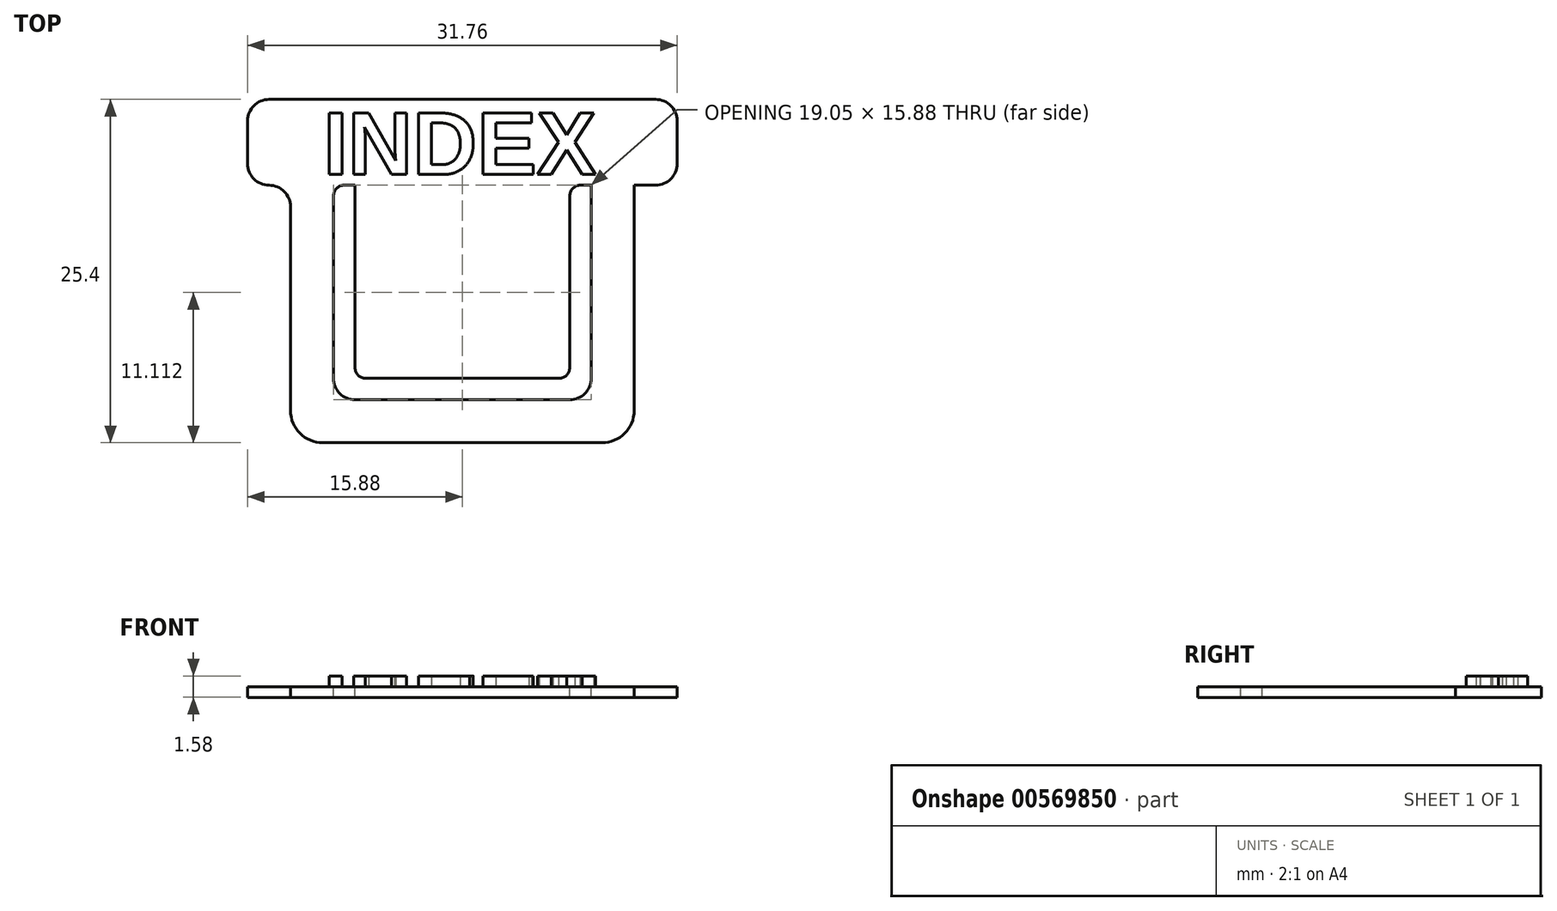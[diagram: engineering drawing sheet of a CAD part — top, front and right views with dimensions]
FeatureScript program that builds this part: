
annotation { "Feature Type Name" : "Feature", "Feature Type Description" : "" }
export const myFeature = defineFeature(function(context is Context, id is Id, definition is map)
    precondition{}
    {
        {
            var Q0;
            Q0=qCreatedBy(makeId("Front.planeOp"),FACE);
            var sketch = newSketch(context, id + "F0", { "sketchPlane" : qUnion([Q0])});
            skLineSegment(sketch, "E0.bottom", {"start": v(12.7, 9.53) * mm, "end": v(-12.7, 9.53) * mm});
            skLineSegment(sketch, "E0.top", {"start": v(12.7, -9.53) * mm, "end": v(-12.7, -9.53) * mm});
            skLineSegment(sketch, "E0.left", {"start": v(12.7, 9.53) * mm, "end": v(12.7, -9.53) * mm});
            skLineSegment(sketch, "E0.right", {"start": v(-12.7, 9.53) * mm, "end": v(-12.7, -9.53) * mm});
            skPoint(sketch, "E0.middle", {"position": v(0, 0) * mm});
            skSolve(sketch);
        }
        {
            var Q0;
            Q0=makeQuery(id+"F0.imprint","IMPRINT",FACE,{"disambiguationData":[TD([[makeQuery(id+"F0.imprint","IMPRINT",EDGE,{"derivedFrom":sQuery(id+"F0.wireOp",EDGE,"E0.bottom")}),1.0]])]});
            extrude(context, id + "F1", {"entities" : qUnion([Q0]), "depth" : 0.8 * mm, "offsetDistance" : 25.4 * mm});
        }
        {
            var Q0;
            Q0=makeQuery(id+"F1.opExtrude","SWEPT_EDGE",EDGE,{"disambiguationData":[OSD([sQuery(id+"F0.wireOp",EDGE,"E0.top"),sQuery(id+"F0.wireOp",EDGE,"E0.left")])]});
            var Q1;
            Q1=makeQuery(id+"F1.opExtrude","SWEPT_EDGE",EDGE,{"disambiguationData":[OSD([sQuery(id+"F0.wireOp",EDGE,"E0.top"),sQuery(id+"F0.wireOp",EDGE,"E0.right")])]});
            fillet(context, id + "F2", {"entities" : qUnion([Q0, Q1]), "radius" : 2.38 * mm, "tangentPropagation" : true, "allowEdgeOverflow" : false});
        }
        {
            var Q0;
            Q0=makeQuery(id+"F1.opExtrude","CAP_FACE",FACE,{"disambiguationData":[OSD([sQuery(id+"F0.wireOp",EDGE,"E0.bottom"),sQuery(id+"F0.wireOp",EDGE,"E0.top"),sQuery(id+"F0.wireOp",EDGE,"E0.left"),sQuery(id+"F0.wireOp",EDGE,"E0.right")])],"isStart":false});
            var sketch = newSketch(context, id + "F3", { "sketchPlane" : qUnion([Q0])});
            skLineSegment(sketch, "E1.bottom", {"start": v(9.52, 9.53) * mm, "end": v(-9.53, 9.53) * mm});
            skLineSegment(sketch, "E1.top", {"start": v(9.53, -6.35) * mm, "end": v(-9.53, -6.35) * mm});
            skLineSegment(sketch, "E1.left", {"start": v(9.52, 9.53) * mm, "end": v(9.53, -6.35) * mm});
            skLineSegment(sketch, "E1.right", {"start": v(-9.53, 9.53) * mm, "end": v(-9.52, -6.35) * mm});
            skPoint(sketch, "E1.middle", {"position": v(0, 0) * mm});
            skSolve(sketch);
        }
        {
            var Q0;
            Q0=makeQuery(id+"F3.imprint","IMPRINT",FACE,{"disambiguationData":[TD([[makeQuery(id+"F3.imprint","IMPRINT",EDGE,{"derivedFrom":sQuery(id+"F3.wireOp",EDGE,"E1.bottom")}),1.0]])]});
            extrude(context, id + "F4", {"entities" : qUnion([Q0]), "operationType" : NewBodyOperationType.REMOVE, "oppositeDirection" : true, "depth" : 4.93 * mm, "offsetDistance" : 25.4 * mm});
        }
        {
            var Q0;
            Q0=makeQuery(id+"F1.opExtrude","CAP_FACE",FACE,{"disambiguationData":[OSD([sQuery(id+"F0.wireOp",EDGE,"E0.bottom"),sQuery(id+"F0.wireOp",EDGE,"E0.top"),sQuery(id+"F0.wireOp",EDGE,"E0.left"),sQuery(id+"F0.wireOp",EDGE,"E0.right")])],"isStart":false});
            var sketch = newSketch(context, id + "F5", { "sketchPlane" : qUnion([Q0])});
            skLineSegment(sketch, "E2.bottom", {"start": v(-15.88, 9.53) * mm, "end": v(15.87, 9.53) * mm});
            skLineSegment(sketch, "E2.top", {"start": v(-15.88, 15.88) * mm, "end": v(15.87, 15.88) * mm});
            skLineSegment(sketch, "E2.left", {"start": v(-15.88, 9.53) * mm, "end": v(-15.88, 15.88) * mm});
            skLineSegment(sketch, "E2.right", {"start": v(15.87, 9.53) * mm, "end": v(15.87, 15.88) * mm});
            skSolve(sketch);
        }
        {
            var Q0;
            Q0=makeQuery(id+"F5.imprint","IMPRINT",FACE,{"disambiguationData":[TD([[makeQuery(id+"F5.imprint","IMPRINT",EDGE,{"derivedFrom":sQuery(id+"F5.wireOp",EDGE,"E2.top")}),-1.0]])]});
            extrude(context, id + "F6", {"entities" : qUnion([Q0]), "operationType" : NewBodyOperationType.ADD, "oppositeDirection" : true, "depth" : 0.8 * mm, "offsetDistance" : 25.4 * mm});
        }
        {
            var Q0;
            Q0=makeQuery(id+"F6.opExtrude","SWEPT_EDGE",EDGE,{"disambiguationData":[OSD([sQuery(id+"F5.wireOp",EDGE,"E2.top"),sQuery(id+"F5.wireOp",EDGE,"E2.left")])]});
            var Q1;
            Q1=makeQuery(id+"F6.opExtrude","SWEPT_EDGE",EDGE,{"disambiguationData":[OSD([sQuery(id+"F5.wireOp",EDGE,"E2.top"),sQuery(id+"F5.wireOp",EDGE,"E2.right")])]});
            var Q2;
            Q2=makeQuery(id+"F6.opExtrude","SWEPT_EDGE",EDGE,{"disambiguationData":[OSD([sQuery(id+"F5.wireOp",EDGE,"E2.bottom"),sQuery(id+"F5.wireOp",EDGE,"E2.right")])]});
            var Q3;
            Q3=makeQuery(id+"F1.opExtrude","SWEPT_EDGE",EDGE,{"disambiguationData":[OSD([sQuery(id+"F0.wireOp",EDGE,"E0.bottom"),sQuery(id+"F0.wireOp",EDGE,"E0.left")])]});
            var Q4;
            Q4=makeQuery(id+"F6.opExtrude","SWEPT_EDGE",EDGE,{"disambiguationData":[OSD([sQuery(id+"F5.wireOp",EDGE,"E2.bottom"),sQuery(id+"F5.wireOp",EDGE,"E2.left")])]});
            var Q5;
            Q5=makeQuery(id+"F1.opExtrude","SWEPT_EDGE",EDGE,{"disambiguationData":[OSD([sQuery(id+"F0.wireOp",EDGE,"E0.bottom"),sQuery(id+"F0.wireOp",EDGE,"E0.right")])]});
            fillet(context, id + "F7", {"entities" : qUnion([Q0, Q1, Q2, Q3, Q4, Q5]), "radius" : 1.59 * mm, "tangentPropagation" : true, "allowEdgeOverflow" : false});
        }
        {
            var Q0;
            Q0=makeQuery(id+"F4.boolean.opBoolean","COPY",EDGE,{"derivedFrom":makeQuery(id+"F4.opExtrude","SWEPT_EDGE",EDGE,{"disambiguationData":[OSD([sQuery(id+"F3.wireOp",EDGE,"E1.top"),sQuery(id+"F3.wireOp",EDGE,"E1.right")])]})});
            var Q1;
            Q1=makeQuery(id+"F4.boolean.opBoolean","COPY",EDGE,{"derivedFrom":makeQuery(id+"F4.opExtrude","SWEPT_EDGE",EDGE,{"disambiguationData":[OSD([sQuery(id+"F3.wireOp",EDGE,"E1.top"),sQuery(id+"F3.wireOp",EDGE,"E1.left")])]})});
            fillet(context, id + "F8", {"entities" : qUnion([Q0, Q1]), "radius" : 1.59 * mm, "tangentPropagation" : true, "allowEdgeOverflow" : false});
        }
        {
            var Q0;
            Q0=makeQuery(id+"F6.boolean.opBoolean","MERGE",FACE,{"derivedFrom":[makeQuery(id+"F1.opExtrude","CAP_FACE",FACE,{"disambiguationData":[OSD([sQuery(id+"F0.wireOp",EDGE,"E0.bottom"),sQuery(id+"F0.wireOp",EDGE,"E0.top"),sQuery(id+"F0.wireOp",EDGE,"E0.left"),sQuery(id+"F0.wireOp",EDGE,"E0.right")])],"isStart":false}),makeQuery(id+"F6.opExtrude","CAP_FACE",FACE,{"disambiguationData":[OSD([sQuery(id+"F5.wireOp",EDGE,"E2.bottom"),sQuery(id+"F5.wireOp",EDGE,"E2.top"),sQuery(id+"F5.wireOp",EDGE,"E2.left"),sQuery(id+"F5.wireOp",EDGE,"E2.right")])],"isStart":true})]});
            var sketch = newSketch(context, id + "F9", { "sketchPlane" : qUnion([Q0])});
            skLineSegment(sketch, "E3.bottom", {"start": v(-7.94, 9.53) * mm, "end": v(7.94, 9.53) * mm});
            skLineSegment(sketch, "E3.top", {"start": v(-7.94, -4.76) * mm, "end": v(7.94, -4.76) * mm});
            skLineSegment(sketch, "E3.left", {"start": v(-7.94, 9.53) * mm, "end": v(-7.94, -4.76) * mm});
            skLineSegment(sketch, "E3.right", {"start": v(7.94, 9.53) * mm, "end": v(7.94, -4.76) * mm});
            skSolve(sketch);
        }
        {
            var Q0;
            Q0=makeQuery(id+"F9.imprint","IMPRINT",FACE,{"disambiguationData":[TD([[makeQuery(id+"F9.imprint","IMPRINT",EDGE,{"derivedFrom":sQuery(id+"F9.wireOp",EDGE,"E3.bottom")}),1.0]])]});
            extrude(context, id + "F10", {"entities" : qUnion([Q0]), "operationType" : NewBodyOperationType.ADD, "oppositeDirection" : true, "depth" : 0.8 * mm, "offsetDistance" : 25.4 * mm});
        }
        {
            var Q0;
            Q0=makeQuery(id+"F10.boolean.opBoolean","MERGE",FACE,{"derivedFrom":[makeQuery(id+"F6.boolean.opBoolean","MERGE",FACE,{"derivedFrom":[makeQuery(id+"F1.opExtrude","CAP_FACE",FACE,{"disambiguationData":[OSD([sQuery(id+"F0.wireOp",EDGE,"E0.bottom"),sQuery(id+"F0.wireOp",EDGE,"E0.top"),sQuery(id+"F0.wireOp",EDGE,"E0.left"),sQuery(id+"F0.wireOp",EDGE,"E0.right")])],"isStart":false}),makeQuery(id+"F6.opExtrude","CAP_FACE",FACE,{"disambiguationData":[OSD([sQuery(id+"F5.wireOp",EDGE,"E2.bottom"),sQuery(id+"F5.wireOp",EDGE,"E2.top"),sQuery(id+"F5.wireOp",EDGE,"E2.left"),sQuery(id+"F5.wireOp",EDGE,"E2.right")])],"isStart":true})]}),makeQuery(id+"F10.opExtrude","CAP_FACE",FACE,{"disambiguationData":[OSD([sQuery(id+"F9.wireOp",EDGE,"E3.bottom"),sQuery(id+"F9.wireOp",EDGE,"E3.top"),sQuery(id+"F9.wireOp",EDGE,"E3.left"),sQuery(id+"F9.wireOp",EDGE,"E3.right")])],"isStart":true})]});
            var sketch = newSketch(context, id + "F11", { "sketchPlane" : qUnion([Q0])});
            skText(sketch, "E4", { "text": "INDEX", "fontName": "Arimo-Bold.ttf"});
            const initialGuessF11  = {"E4": [-0.0103, 0.01032, 1, 0, 0.00476]};
            skSetInitialGuess(sketch, initialGuessF11);
            skSolve(sketch);
        }
        {
            var Q0;
            Q0=qSketchRegion(id+"F11",true);
            extrude(context, id + "F12", {"entities" : qUnion([Q0]), "operationType" : NewBodyOperationType.ADD, "depth" : 0.8 * mm, "offsetDistance" : 25.4 * mm});
        }
        {
            var Q0;
            Q0=makeQuery(id+"F10.opExtrude","SWEPT_EDGE",EDGE,{"disambiguationData":[OSD([sQuery(id+"F5.wireOp",EDGE,"E2.bottom"),sQuery(id+"F9.wireOp",EDGE,"E3.bottom"),sQuery(id+"F9.wireOp",EDGE,"E3.left")])]});
            var Q1;
            Q1=makeQuery(id+"F4.boolean.opBoolean","COPY",EDGE,{"derivedFrom":makeQuery(id+"F4.opExtrude","SWEPT_EDGE",EDGE,{"disambiguationData":[OSD([sQuery(id+"F0.wireOp",EDGE,"E0.bottom"),sQuery(id+"F3.wireOp",EDGE,"E1.bottom"),sQuery(id+"F3.wireOp",EDGE,"E1.right")])]})});
            var Q2;
            Q2=makeQuery(id+"F10.opExtrude","SWEPT_EDGE",EDGE,{"disambiguationData":[OSD([sQuery(id+"F5.wireOp",EDGE,"E2.bottom"),sQuery(id+"F9.wireOp",EDGE,"E3.bottom"),sQuery(id+"F9.wireOp",EDGE,"E3.right")])]});
            var Q3;
            Q3=makeQuery(id+"F4.boolean.opBoolean","COPY",EDGE,{"derivedFrom":makeQuery(id+"F4.opExtrude","SWEPT_EDGE",EDGE,{"disambiguationData":[OSD([sQuery(id+"F0.wireOp",EDGE,"E0.bottom"),sQuery(id+"F3.wireOp",EDGE,"E1.bottom"),sQuery(id+"F3.wireOp",EDGE,"E1.left")])]})});
            fillet(context, id + "F13", {"entities" : qUnion([Q0, Q1, Q2, Q3]), "radius" : 0.8 * mm, "tangentPropagation" : true, "allowEdgeOverflow" : false});
        }
        {
            var Q0;
            Q0=makeQuery(id+"F10.opExtrude","SWEPT_EDGE",EDGE,{"disambiguationData":[OSD([sQuery(id+"F9.wireOp",EDGE,"E3.top"),sQuery(id+"F9.wireOp",EDGE,"E3.left")])]});
            var Q1;
            Q1=makeQuery(id+"F10.opExtrude","SWEPT_EDGE",EDGE,{"disambiguationData":[OSD([sQuery(id+"F9.wireOp",EDGE,"E3.top"),sQuery(id+"F9.wireOp",EDGE,"E3.right")])]});
            fillet(context, id + "F14", {"entities" : qUnion([Q0, Q1]), "radius" : 0.8 * mm, "tangentPropagation" : true, "allowEdgeOverflow" : false});
        }
        {
            var Q0;
            Q0=makeQuery(id+"F1.opExtrude","SWEPT_BODY",BODY,{"disambiguationData":[OSD([sQuery(id+"F0.wireOp",EDGE,"E0.bottom"),sQuery(id+"F0.wireOp",EDGE,"E0.top"),sQuery(id+"F0.wireOp",EDGE,"E0.left"),sQuery(id+"F0.wireOp",EDGE,"E0.right")])]});
            var Q1;
            Q1=makeQuery(id+"F6.opExtrude","CAP_EDGE",EDGE,{"disambiguationData":[OSD([sQuery(id+"F5.wireOp",EDGE,"E2.top")])],"isStart":false});
            transform(context, id + "F15", {"entities" : qUnion([Q0]), "transformType" : TransformType.ROTATION, "transformAxis" : qUnion([Q1]), "angle" : 270 * degree, "makeCopy" : false});
        }
    });
